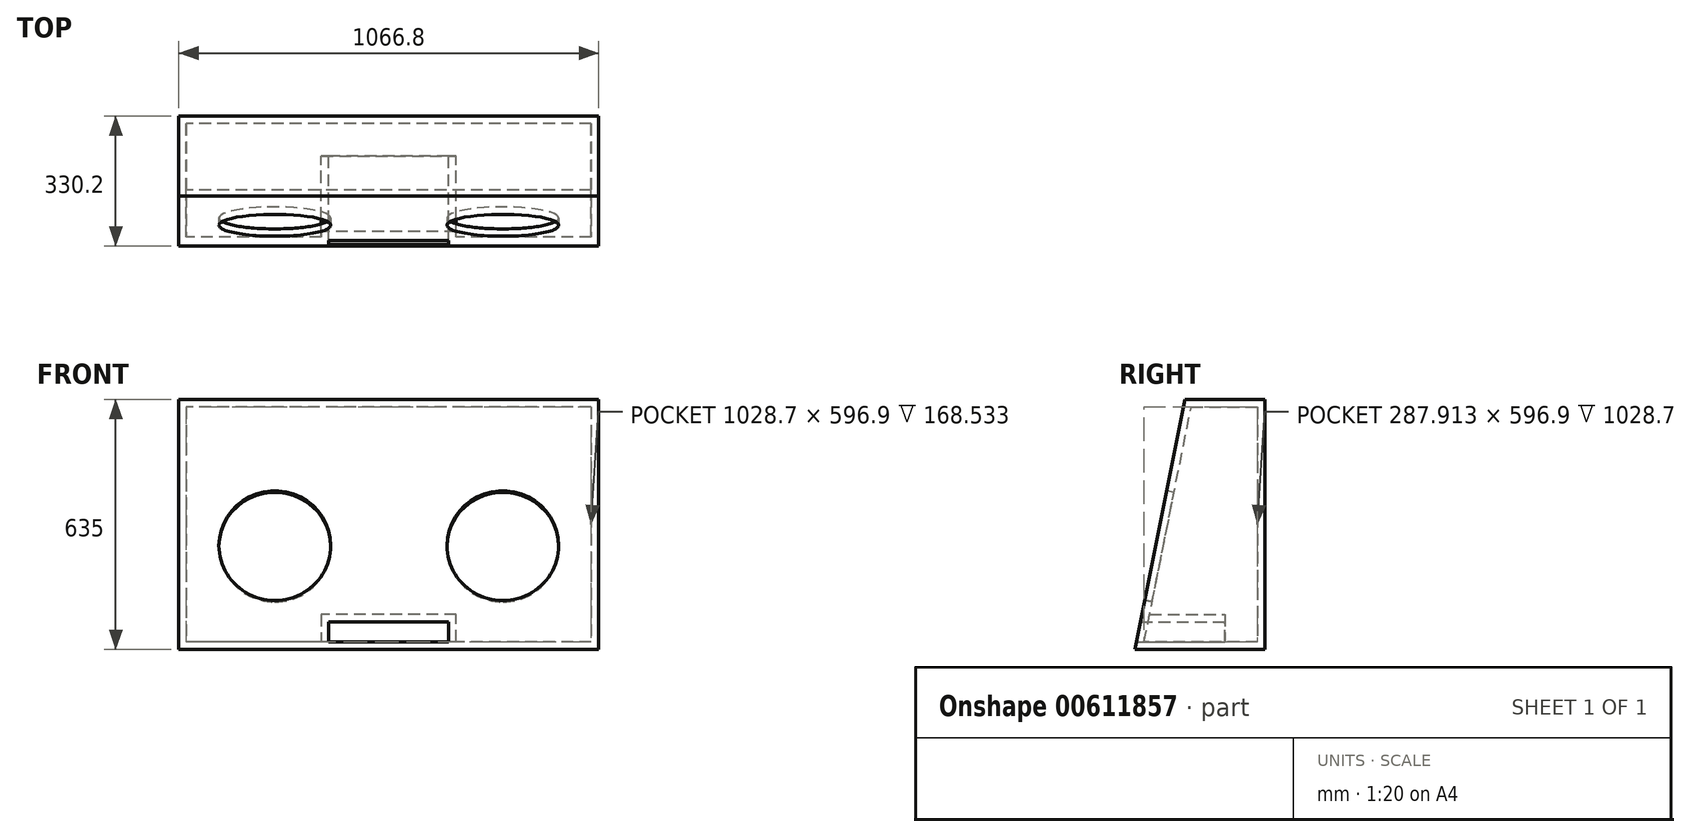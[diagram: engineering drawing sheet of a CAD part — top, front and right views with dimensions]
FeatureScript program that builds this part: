
annotation { "Feature Type Name" : "Feature", "Feature Type Description" : "" }
export const myFeature = defineFeature(function(context is Context, id is Id, definition is map)
    precondition{}
    {
        {
            var Q0;
            Q0=qCreatedBy(makeId("Right.planeOp"),FACE);
            var sketch = newSketch(context, id + "F0", { "sketchPlane" : qUnion([Q0])});
            skLineSegment(sketch, "E0", {"start": v(0, 0) * mm, "end": v(-330.2, 0) * mm});
            skLineSegment(sketch, "E1", {"start": v(-330.2, 0) * mm, "end": v(-203.2, 635) * mm});
            skLineSegment(sketch, "E2", {"start": v(-203.2, 635) * mm, "end": v(0, 635) * mm});
            skLineSegment(sketch, "E3", {"start": v(0, 635) * mm, "end": v(0, 0) * mm});
            skSolve(sketch);
        }
        {
            var Q0;
            Q0 = qSketchRegion(id + "F0", true);
            extrude(context, id + "F1", {"entities" : qUnion([Q0]), "depth" : 533.4 * mm, "offsetDistance" : 25.4 * mm, "hasSecondDirection" : true, "secondDirectionOppositeDirection" : true, "secondDirectionDepth" : 533.4 * mm});
        }
        {
            var Q0;
            Q0=qCreatedBy(makeId("Front.planeOp"),FACE);
            cPlane(context, id + "F2", {"entities" : qUnion([Q0]), "cplaneType" : CPlaneType.OFFSET, "offset" : 25.4 * mm, "width" : 152.4 * mm, "height" : 152.4 * mm});
        }
        {
            var Q0;
            Q0=qCreatedBy(id+"F2.planeOp",FACE);
            var sketch = newSketch(context, id + "F3", { "sketchPlane" : qUnion([Q0])});
            skLineSegment(sketch, "E4.bottom", {"start": v(-152.4, 69.85) * mm, "end": v(152.4, 69.85) * mm});
            skLineSegment(sketch, "E4.top", {"start": v(-152.4, 19.05) * mm, "end": v(152.4, 19.05) * mm});
            skLineSegment(sketch, "E4.left", {"start": v(-152.4, 69.85) * mm, "end": v(-152.4, 19.05) * mm});
            skLineSegment(sketch, "E4.right", {"start": v(152.4, 69.85) * mm, "end": v(152.4, 19.05) * mm});
            skSolve(sketch);
        }
        {
            var Q0;
            Q0 = qSketchRegion(id + "F3", true);
            extrude(context, id + "F4", {"entities" : qUnion([Q0]), "operationType" : NewBodyOperationType.REMOVE, "endBound" : BoundingType.THROUGH_ALL, "depth" : 25.4 * mm, "offsetDistance" : 25.4 * mm});
        }
        {
            var Q0;
            Q0=makeQuery(id+"F4.boolean.opBoolean","COPY",FACE,{"derivedFrom":makeQuery(id+"F4.opExtrude","SWEPT_FACE",FACE,{"disambiguationData":[OSD([sQuery(id+"F3.wireOp",EDGE,"E4.left")])]})});
            var Q1;
            Q1=makeQuery(id+"F4.boolean.opBoolean","COPY",FACE,{"derivedFrom":makeQuery(id+"F4.opExtrude","SWEPT_FACE",FACE,{"disambiguationData":[OSD([sQuery(id+"F3.wireOp",EDGE,"E4.bottom")])]})});
            var Q2;
            Q2=makeQuery(id+"F4.boolean.opBoolean","COPY",FACE,{"derivedFrom":makeQuery(id+"F4.opExtrude","SWEPT_FACE",FACE,{"disambiguationData":[OSD([sQuery(id+"F3.wireOp",EDGE,"E4.right")])]})});
            shell(context, id + "F5", {"entities" : qUnion([Q0, Q1, Q2]), "thickness" : 19.05 * mm});
        }
        {
            var Q0;
            Q0=makeQuery(id+"F1.opExtrude","SWEPT_FACE",FACE,{"disambiguationData":[OSD([sQuery(id+"F0.wireOp",EDGE,"E1")])]});
            var sketch = newSketch(context, id + "F6", { "sketchPlane" : qUnion([Q0])});
            skCircle(sketch, "E5", {"center": v(-289.72, 204.32) * mm, "radius": 142.08 * mm});
            skCircle(sketch, "E6", {"center": v(289.72, 204.32) * mm, "radius": 142.08 * mm});
            skSolve(sketch);
        }
        {
            var Q0;
            Q0 = qSketchRegion(id + "F6", true);
            extrude(context, id + "F7", {"entities" : qUnion([Q0]), "operationType" : NewBodyOperationType.REMOVE, "oppositeDirection" : true, "depth" : 50.8 * mm, "offsetDistance" : 25.4 * mm});
        }
        {
            var Q0;
            Q0=makeQuery(id+"F4.boolean.opBoolean","COPY",FACE,{"derivedFrom":makeQuery(id+"F4.opExtrude","CAP_FACE",FACE,{"disambiguationData":[OSD([sQuery(id+"F3.wireOp",EDGE,"E4.bottom"),sQuery(id+"F3.wireOp",EDGE,"E4.top"),sQuery(id+"F3.wireOp",EDGE,"E4.left"),sQuery(id+"F3.wireOp",EDGE,"E4.right")])],"isStart":true})});
            var sketch = newSketch(context, id + "F8", { "sketchPlane" : qUnion([Q0])});
            skSolve(sketch);
        }
        {
            var Q0;
            Q0=makeQuery(id+"F8.imprint","IMPRINT",FACE,{"disambiguationData":[TD([[makeQuery(id+"F8.imprint","IMPRINT",EDGE,{"derivedFrom":makeQuery(id+"F4.boolean.opBoolean","COPY",EDGE,{"derivedFrom":makeQuery(id+"F4.opExtrude","CAP_EDGE",EDGE,{"disambiguationData":[OSD([sQuery(id+"F3.wireOp",EDGE,"E4.top")])],"isStart":true})})}),1.0]])]});
            var Q1;
            Q1=makeQuery(id+"F5.opShell","OFFSET_FACE",FACE,{"disambiguationData":[OSD([sQuery(id+"F0.wireOp",EDGE,"E3")])]});
            extrude(context, id + "F9", {"entities" : qUnion([Q0]), "operationType" : NewBodyOperationType.REMOVE, "endBound" : BoundingType.UP_TO_SURFACE, "oppositeDirection" : true, "depth" : 25.4 * mm, "endBoundEntityFace" : qUnion([Q1]), "offsetDistance" : 25.4 * mm});
        }
        {
            var Q0;
            Q0=qCreatedBy(makeId("Front.planeOp"),FACE);
            cPlane(context, id + "F10", {"entities" : qUnion([Q0]), "cplaneType" : CPlaneType.OFFSET, "offset" : 101.6 * mm, "width" : 152.4 * mm, "height" : 152.4 * mm});
        }
        {
            var Q0;
            Q0=qCreatedBy(id+"F10.planeOp",FACE);
            var sketch = newSketch(context, id + "F11", { "sketchPlane" : qUnion([Q0])});
            skLineSegment(sketch, "E7", {"start": v(-152.4, 19.05) * mm, "end": v(-171.45, 19.05) * mm});
            skLineSegment(sketch, "E8", {"start": v(-171.45, 19.05) * mm, "end": v(-171.45, 88.9) * mm});
            skLineSegment(sketch, "E9", {"start": v(-171.45, 88.9) * mm, "end": v(171.45, 88.9) * mm});
            skLineSegment(sketch, "E10", {"start": v(171.45, 88.9) * mm, "end": v(171.45, 19.05) * mm});
            skLineSegment(sketch, "E11", {"start": v(171.45, 19.05) * mm, "end": v(152.4, 19.05) * mm});
            skLineSegment(sketch, "E12", {"start": v(152.4, 19.05) * mm, "end": v(152.4, 69.85) * mm});
            skLineSegment(sketch, "E13", {"start": v(152.4, 69.85) * mm, "end": v(-152.4, 69.85) * mm});
            skLineSegment(sketch, "E14", {"start": v(-152.4, 69.85) * mm, "end": v(-152.4, 19.05) * mm});
            skSolve(sketch);
        }
        {
            var Q0;
            Q0 = qSketchRegion(id + "F11", true);
            var Q1;
            Q1=makeQuery(id+"F1.opExtrude","SWEPT_FACE",FACE,{"disambiguationData":[OSD([sQuery(id+"F0.wireOp",EDGE,"E1")])]});
            extrude(context, id + "F12", {"entities" : qUnion([Q0]), "operationType" : NewBodyOperationType.ADD, "endBound" : BoundingType.UP_TO_SURFACE, "depth" : 25.4 * mm, "endBoundEntityFace" : qUnion([Q1]), "offsetDistance" : 25.4 * mm});
        }
    });
